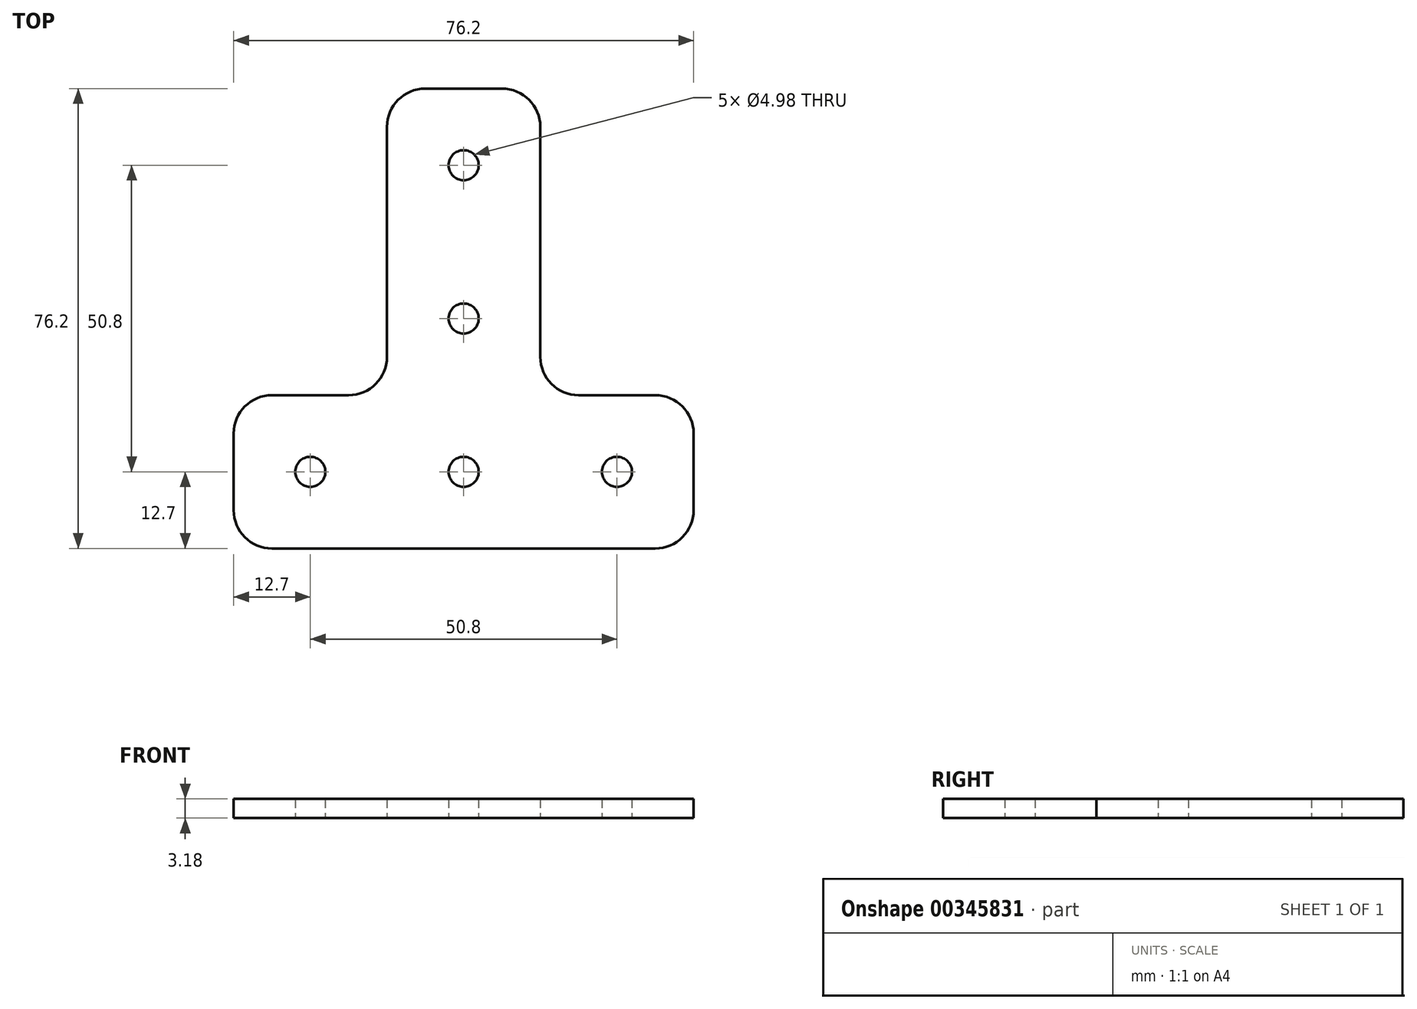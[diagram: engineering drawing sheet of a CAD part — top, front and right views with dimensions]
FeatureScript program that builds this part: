
annotation { "Feature Type Name" : "Feature", "Feature Type Description" : "" }
export const myFeature = defineFeature(function(context is Context, id is Id, definition is map)
    precondition{}
    {
        {
            var Q0;
            Q0=qCreatedBy(makeId("Top.planeOp"),FACE);
            var sketch = newSketch(context, id + "F0", { "sketchPlane" : qUnion([Q0])});
            skCircle(sketch, "E0", {"center": v(0, 0) * mm, "radius": 2.49 * mm});
            skLineSegment(sketch, "E1", {"start": v(-25.4, 0) * mm, "end": v(25.4, 0) * mm, "construction": true});
            skCircle(sketch, "E2", {"center": v(-25.4, 0) * mm, "radius": 2.49 * mm});
            skCircle(sketch, "E3", {"center": v(25.4, 0) * mm, "radius": 2.49 * mm});
            skLineSegment(sketch, "E4", {"start": v(0, 0) * mm, "end": v(0, 50.8) * mm, "construction": true});
            skCircle(sketch, "E5", {"center": v(0, 50.8) * mm, "radius": 2.49 * mm});
            skCircle(sketch, "E6", {"center": v(0, 25.4) * mm, "radius": 2.49 * mm});
            skLineSegment(sketch, "E7", {"start": v(-38.1, -12.7) * mm, "end": v(38.1, -12.7) * mm});
            skLineSegment(sketch, "E8", {"start": v(38.1, -12.7) * mm, "end": v(38.1, 12.7) * mm});
            skLineSegment(sketch, "E9", {"start": v(38.1, 12.7) * mm, "end": v(12.7, 12.7) * mm});
            skLineSegment(sketch, "E10", {"start": v(12.7, 12.7) * mm, "end": v(12.7, 63.5) * mm});
            skLineSegment(sketch, "E11", {"start": v(12.7, 63.5) * mm, "end": v(-12.7, 63.5) * mm});
            skLineSegment(sketch, "E12", {"start": v(-12.7, 63.5) * mm, "end": v(-12.7, 12.7) * mm});
            skLineSegment(sketch, "E13", {"start": v(-12.7, 12.7) * mm, "end": v(-38.1, 12.7) * mm});
            skLineSegment(sketch, "E14", {"start": v(-38.1, 12.7) * mm, "end": v(-38.1, -12.7) * mm});
            skSolve(sketch);
        }
        {
            var Q0;
            Q0 = qSketchRegion(id + "F0", true);
            extrude(context, id + "F1", {"entities" : qUnion([Q0]), "endBound" : BoundingType.SYMMETRIC, "depth" : 3.17 * mm});
        }
        {
            var Q0;
            Q0=makeQuery(id+"F1.opExtrude","SWEPT_EDGE",EDGE,{"disambiguationData":[OSD([sQuery(id+"F0.wireOp",EDGE,"E12"),sQuery(id+"F0.wireOp",EDGE,"E13")])]});
            var Q1;
            Q1=makeQuery(id+"F1.opExtrude","SWEPT_EDGE",EDGE,{"disambiguationData":[OSD([sQuery(id+"F0.wireOp",EDGE,"E11"),sQuery(id+"F0.wireOp",EDGE,"E12")])]});
            var Q2;
            Q2=makeQuery(id+"F1.opExtrude","SWEPT_EDGE",EDGE,{"disambiguationData":[OSD([sQuery(id+"F0.wireOp",EDGE,"E10"),sQuery(id+"F0.wireOp",EDGE,"E11")])]});
            var Q3;
            Q3=makeQuery(id+"F1.opExtrude","SWEPT_EDGE",EDGE,{"disambiguationData":[OSD([sQuery(id+"F0.wireOp",EDGE,"E9"),sQuery(id+"F0.wireOp",EDGE,"E10")])]});
            var Q4;
            Q4=makeQuery(id+"F1.opExtrude","SWEPT_EDGE",EDGE,{"disambiguationData":[OSD([sQuery(id+"F0.wireOp",EDGE,"E8"),sQuery(id+"F0.wireOp",EDGE,"E9")])]});
            var Q5;
            Q5=makeQuery(id+"F1.opExtrude","SWEPT_EDGE",EDGE,{"disambiguationData":[OSD([sQuery(id+"F0.wireOp",EDGE,"E7"),sQuery(id+"F0.wireOp",EDGE,"E8")])]});
            var Q6;
            Q6=makeQuery(id+"F1.opExtrude","SWEPT_EDGE",EDGE,{"disambiguationData":[OSD([sQuery(id+"F0.wireOp",EDGE,"E7"),sQuery(id+"F0.wireOp",EDGE,"E14")])]});
            var Q7;
            Q7=makeQuery(id+"F1.opExtrude","SWEPT_EDGE",EDGE,{"disambiguationData":[OSD([sQuery(id+"F0.wireOp",EDGE,"E13"),sQuery(id+"F0.wireOp",EDGE,"E14")])]});
            fillet(context, id + "F2", {"entities" : qUnion([Q0, Q1, Q2, Q3, Q4, Q5, Q6, Q7]), "radius" : 6.35 * mm, "tangentPropagation" : true, "allowEdgeOverflow" : false});
        }
    });
